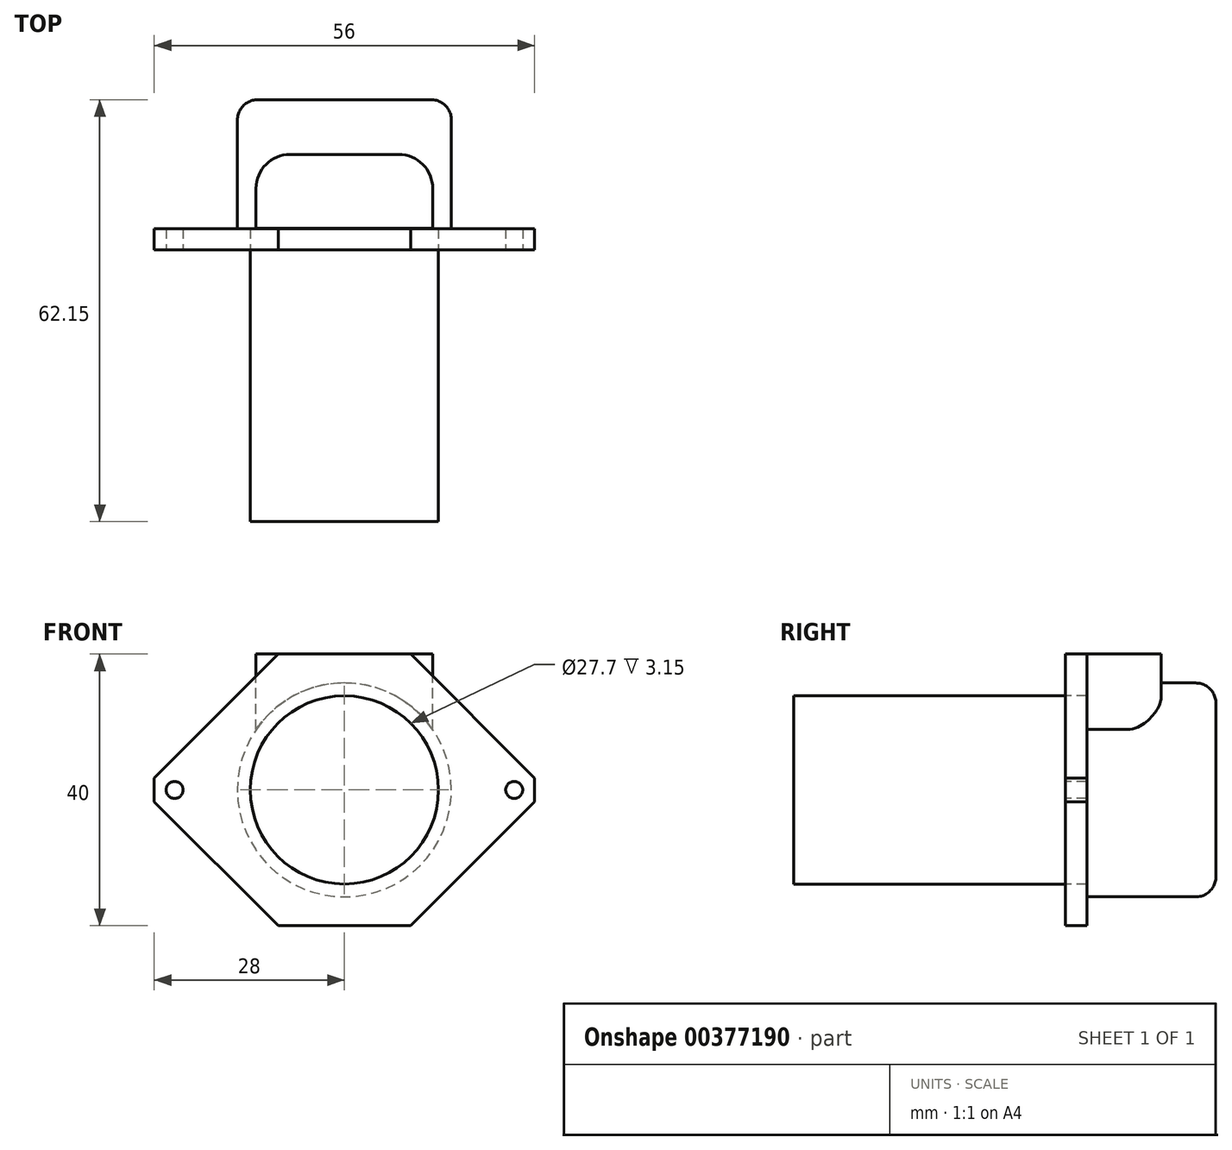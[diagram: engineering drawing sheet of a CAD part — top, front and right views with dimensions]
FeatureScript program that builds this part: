
annotation { "Feature Type Name" : "Feature", "Feature Type Description" : "" }
export const myFeature = defineFeature(function(context is Context, id is Id, definition is map)
    precondition{}
    {
        {
            var Q0;
            Q0=qCreatedBy(makeId("Front.planeOp"),FACE);
            var sketch = newSketch(context, id + "F0", { "sketchPlane" : qUnion([Q0])});
            skLineSegment(sketch, "E0", {"start": v(-28, 1.75) * mm, "end": v(-9.75, 20) * mm});
            skLineSegment(sketch, "E1", {"start": v(-9.75, 20) * mm, "end": v(9.75, 20) * mm});
            skLineSegment(sketch, "E2", {"start": v(9.75, 20) * mm, "end": v(28, 1.75) * mm});
            skLineSegment(sketch, "E3", {"start": v(28, -1.75) * mm, "end": v(9.75, -20) * mm});
            skLineSegment(sketch, "E4", {"start": v(9.75, -20) * mm, "end": v(-9.75, -20) * mm});
            skLineSegment(sketch, "E5", {"start": v(-9.75, -20) * mm, "end": v(-28, -1.75) * mm});
            skLineSegment(sketch, "E6", {"start": v(28, 1.75) * mm, "end": v(28, -1.75) * mm});
            skLineSegment(sketch, "E7", {"start": v(-28, 1.75) * mm, "end": v(-28, -1.75) * mm});
            skPoint(sketch, "E8.orphan", {"position": v(-29.75, 0) * mm});
            skPoint(sketch, "E9.orphan", {"position": v(29.75, 0) * mm});
            skLineSegment(sketch, "E10", {"start": v(0, 0) * mm, "end": v(25, 0) * mm, "construction": true});
            skLineSegment(sketch, "E11", {"start": v(0, 0) * mm, "end": v(-25, 0) * mm, "construction": true});
            skCircle(sketch, "E12", {"center": v(-25, 0) * mm, "radius": 1.25 * mm});
            skCircle(sketch, "E13", {"center": v(25, 0) * mm, "radius": 1.25 * mm});
            skCircle(sketch, "E14", {"center": v(0, 0) * mm, "radius": 13.85 * mm});
            skSolve(sketch);
        }
        {
            var Q0;
            Q0=makeQuery(id+"F0.imprint","IMPRINT",FACE,{"disambiguationData":[TD([[makeQuery(id+"F0.imprint","IMPRINT",EDGE,{"derivedFrom":sQuery(id+"F0.wireOp",EDGE,"E0")}),-1.0]])]});
            extrude(context, id + "F1", {"entities" : qUnion([Q0]), "oppositeDirection" : true, "depth" : 3.15 * mm});
        }
        {
            var Q0;
            Q0=makeQuery(id+"F0.imprint","IMPRINT",FACE,{"disambiguationData":[TD([[makeQuery(id+"F0.imprint","IMPRINT",EDGE,{"derivedFrom":sQuery(id+"F0.wireOp",EDGE,"E14")}),1.0]])]});
            extrude(context, id + "F2", {"entities" : qUnion([Q0]), "depth" : 40 * mm});
        }
        {
            var Q0;
            Q0=makeQuery(id+"F1.opExtrude","CAP_FACE",FACE,{"disambiguationData":[OSD([sQuery(id+"F0.wireOp",EDGE,"E0"),sQuery(id+"F0.wireOp",EDGE,"E1"),sQuery(id+"F0.wireOp",EDGE,"E2"),sQuery(id+"F0.wireOp",EDGE,"E3"),sQuery(id+"F0.wireOp",EDGE,"E4"),sQuery(id+"F0.wireOp",EDGE,"E5"),sQuery(id+"F0.wireOp",EDGE,"E6"),sQuery(id+"F0.wireOp",EDGE,"E7"),sQuery(id+"F0.wireOp",EDGE,"E12"),sQuery(id+"F0.wireOp",EDGE,"E13"),sQuery(id+"F0.wireOp",EDGE,"E14")])],"isStart":false});
            var sketch = newSketch(context, id + "F3", { "sketchPlane" : qUnion([Q0])});
            skCircle(sketch, "E15", {"center": v(0, 0) * mm, "radius": 15.75 * mm});
            skSolve(sketch);
        }
        {
            var Q0;
            Q0 = qSketchRegion(id + "F3", true);
            extrude(context, id + "F4", {"entities" : qUnion([Q0]), "operationType" : NewBodyOperationType.ADD, "depth" : 19 * mm});
        }
        {
            var Q0;
            Q0=makeQuery(id+"F4.opExtrude","CAP_EDGE",EDGE,{"disambiguationData":[OSD([sQuery(id+"F3.wireOp",EDGE,"E15")])],"isStart":false});
            fillet(context, id + "F5", {"entities" : qUnion([Q0]), "radius" : 3 * mm, "tangentPropagation" : true, "allowEdgeOverflow" : false});
        }
        {
            var Q0;
            Q0=makeQuery(id+"F1.opExtrude","SWEPT_FACE",FACE,{"disambiguationData":[OSD([sQuery(id+"F0.wireOp",EDGE,"E1")])]});
            var sketch = newSketch(context, id + "F6", { "sketchPlane" : qUnion([Q0])});
            skLineSegment(sketch, "E16.bottom", {"start": v(-13, 14.08) * mm, "end": v(13, 14.08) * mm});
            skLineSegment(sketch, "E16.top", {"start": v(-13, 3.18) * mm, "end": v(13, 3.18) * mm});
            skLineSegment(sketch, "E16.left", {"start": v(-13, 14.08) * mm, "end": v(-13, 3.18) * mm});
            skLineSegment(sketch, "E16.right", {"start": v(13, 14.08) * mm, "end": v(13, 3.18) * mm});
            skPoint(sketch, "E16.middle", {"position": v(0, 8.63) * mm});
            skSolve(sketch);
        }
        {
            var Q0;
            Q0=makeQuery(id+"F6.imprint","IMPRINT",FACE,{"disambiguationData":[TD([[makeQuery(id+"F6.imprint","IMPRINT",EDGE,{"derivedFrom":sQuery(id+"F6.wireOp",EDGE,"E16.bottom")}),-1.0]])]});
            extrude(context, id + "F7", {"entities" : qUnion([Q0]), "operationType" : NewBodyOperationType.ADD, "oppositeDirection" : true, "depth" : 12 * mm});
        }
        {
            var Q0;
            Q0=makeQuery(id+"F7.opExtrude","SWEPT_EDGE",EDGE,{"disambiguationData":[OSD([sQuery(id+"F6.wireOp",EDGE,"E16.bottom"),sQuery(id+"F6.wireOp",EDGE,"E16.right")])]});
            var Q1;
            Q1=makeQuery(id+"F7.opExtrude","SWEPT_EDGE",EDGE,{"disambiguationData":[OSD([sQuery(id+"F6.wireOp",EDGE,"E16.bottom"),sQuery(id+"F6.wireOp",EDGE,"E16.left")])]});
            fillet(context, id + "F8", {"entities" : qUnion([Q0, Q1]), "radius" : 5 * mm, "tangentPropagation" : true, "allowEdgeOverflow" : false});
        }
    });
